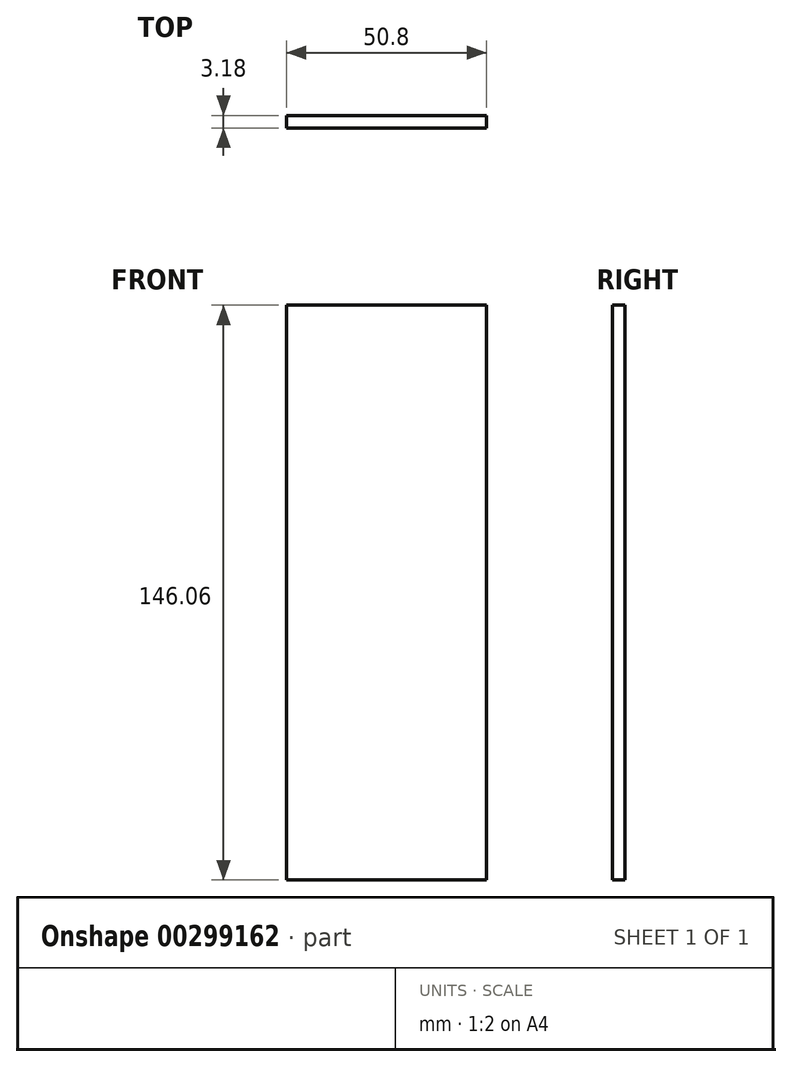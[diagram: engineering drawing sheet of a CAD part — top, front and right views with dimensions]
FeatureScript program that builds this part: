
annotation { "Feature Type Name" : "Feature", "Feature Type Description" : "" }
export const myFeature = defineFeature(function(context is Context, id is Id, definition is map)
    precondition{}
    {
        {
            var Q0;
            Q0=qCreatedBy(makeId("Front.planeOp"),FACE);
            var sketch = newSketch(context, id + "F0", { "sketchPlane" : qUnion([Q0])});
            skLineSegment(sketch, "E0.bottom", {"start": v(-25.4, 73.02) * mm, "end": v(25.4, 73.02) * mm});
            skLineSegment(sketch, "E0.top", {"start": v(-25.4, -73.03) * mm, "end": v(25.4, -73.03) * mm});
            skLineSegment(sketch, "E0.left", {"start": v(-25.4, 73.02) * mm, "end": v(-25.4, -73.03) * mm});
            skLineSegment(sketch, "E0.right", {"start": v(25.4, 73.02) * mm, "end": v(25.4, -73.03) * mm});
            skPoint(sketch, "E0.middle", {"position": v(0, 0) * mm});
            skSolve(sketch);
        }
        {
            var Q0;
            Q0 = qSketchRegion(id + "F0", true);
            extrude(context, id + "F1", {"entities" : qUnion([Q0]), "endBound" : BoundingType.SYMMETRIC, "depth" : 3.17 * mm});
        }
    });
